# Revit family: TUSL20
name_source: partatom
category: Structural Connections
revit_build: Autodesk Revit 2015 (Build: 20140606_1530(x64)
units: mm (PartAtom-declared; Revit-internal decimal feet)

## types (1)
- TUSL20
    Default Elevation = 0 mm  [stored 0 ft]
    Density = 0.53 kg
    Description = Concealed beam hanger
    EPD = https://www.strongtie.eu
    ETA / DoP = https://www.strongtie.eu
    H = 174 mm  [stored 0.570866 ft]
    Manufacturer = Simpson Strong-Tie
    Model = TUSL20
    Model Disclaimer = Contact Simpson Strong-Tie Company  for more information
    Model ID = 0257240673103386342518303183791017523502
    Name = TUSL20
    ObjectType = TUSL20
    Product Material = Galvanised
    Product Type = Concealed beam hanger
    Reference = TUSL20
    STD type1 = STD12X60
    STD type2 = STD12X80
    STD type3 = STD12X100
    STD type4 = STD12X120
    Technical datasheet = https://www.strongtie.eu
    URL = www.strongtie.eu
    UniClass Number = Pr_20_29_31_13
    UniClass Title = Carbon steel punched metal plate fasteners
    W = 60 mm  [stored 0.19685 ft]

note: [stored X ft] marks values corroborated as IEEE doubles in the binary element streams (Revit-internal decimal feet)

## geometry (parser evidence)
native form markers: Blend x35, Sweep x15
no freeform markers — native parametric forms only
